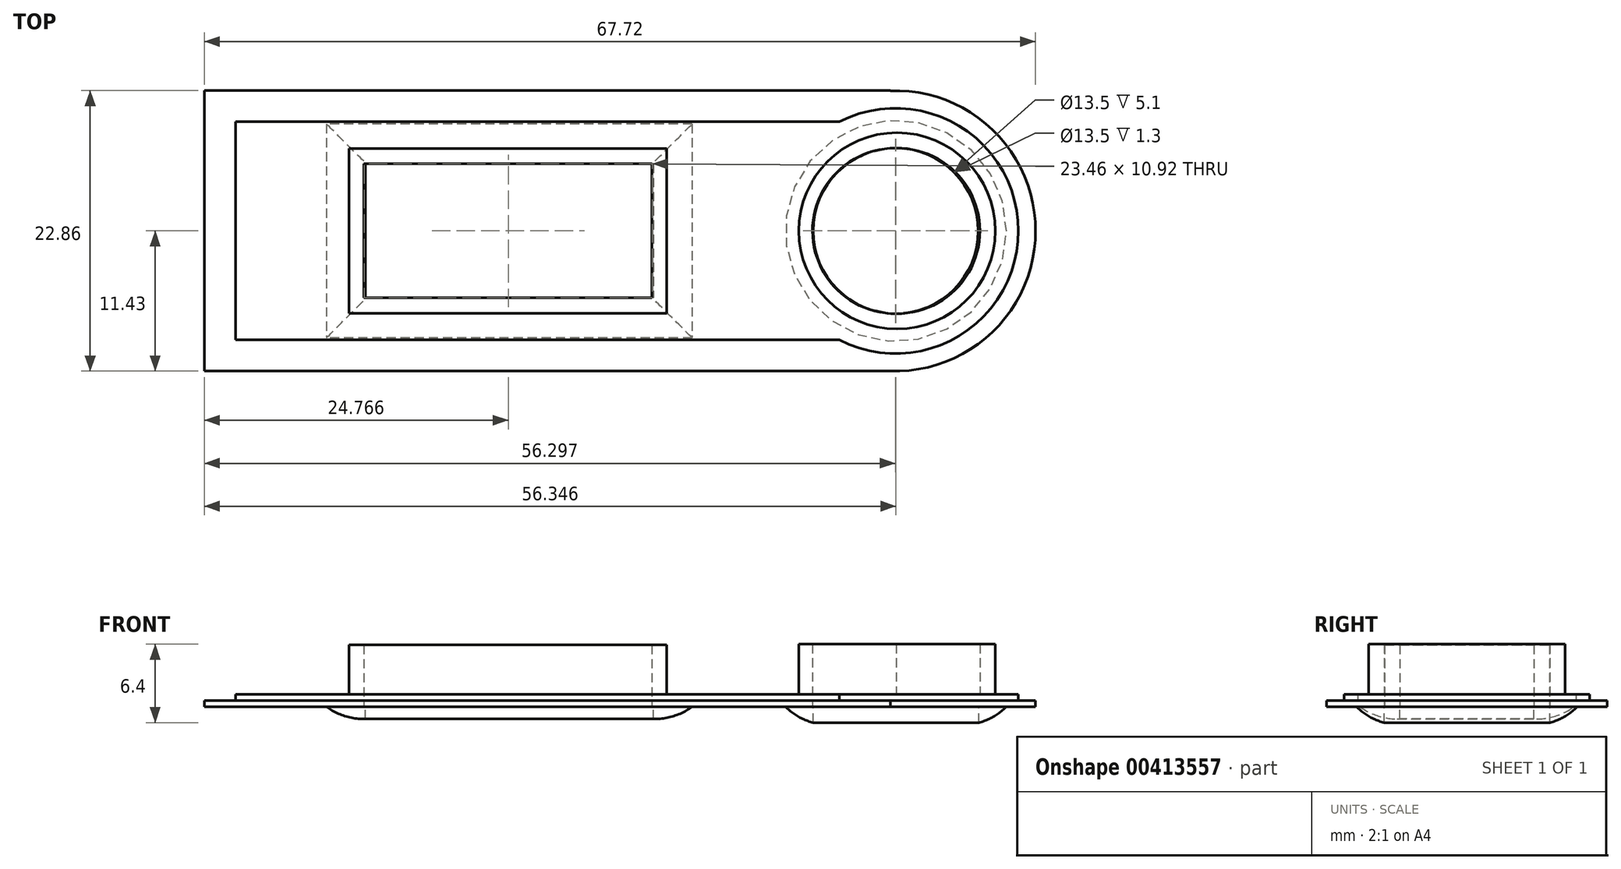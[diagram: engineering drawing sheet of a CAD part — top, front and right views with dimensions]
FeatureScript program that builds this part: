
annotation { "Feature Type Name" : "Feature", "Feature Type Description" : "" }
export const myFeature = defineFeature(function(context is Context, id is Id, definition is map)
    precondition{}
    {
        {
            var Q0;
            Q0=qCreatedBy(makeId("Top.planeOp"),FACE);
            var sketch = newSketch(context, id + "F0", { "sketchPlane" : qUnion([Q0])});
            skLineSegment(sketch, "E0.bottom", {"start": v(25.4, -8.9) * mm, "end": v(-25.4, -8.9) * mm});
            skLineSegment(sketch, "E0.top", {"start": v(25.4, 8.9) * mm, "end": v(-25.4, 8.89) * mm});
            skLineSegment(sketch, "E0.left", {"start": v(25.4, -8.9) * mm, "end": v(25.4, 8.9) * mm});
            skLineSegment(sketch, "E0.right", {"start": v(-25.4, -8.9) * mm, "end": v(-25.4, 8.89) * mm});
            skPoint(sketch, "E0.middle", {"position": v(0, 0) * mm});
            skSolve(sketch);
        }
        {
            var Q0;
            Q0=qCreatedBy(makeId("Top.planeOp"),FACE);
            var sketch = newSketch(context, id + "F1", { "sketchPlane" : qUnion([Q0])});
            skCircle(sketch, "E1", {"center": v(28.38, 0) * mm, "radius": 10 * mm});
            skSolve(sketch);
        }
        {
            var Q0;
            Q0=qSketchRegion(id+"F0",true);
            var Q1;
            Q1=qSketchRegion(id+"F18",true);
            extrude(context, id + "F2", {"entities" : qUnion([Q0, Q1]), "depth" : 1.02 * mm});
        }
        {
            var Q0;
            Q0=makeQuery(id+"F1.imprint","IMPRINT",FACE,{"disambiguationData":[TD([[makeQuery(id+"F1.imprint","IMPRINT",EDGE,{"derivedFrom":sQuery(id+"F1.wireOp",EDGE,"E1")}),1.0]])]});
            extrude(context, id + "F3", {"entities" : qUnion([Q0]), "operationType" : NewBodyOperationType.ADD, "depth" : 1.02 * mm});
        }
        {
            var Q0;
            Q0=qCreatedBy(makeId("Top.planeOp"),FACE);
            var sketch = newSketch(context, id + "F4", { "sketchPlane" : qUnion([Q0])});
            skCircle(sketch, "E2", {"center": v(28.36, 0) * mm, "radius": 6.75 * mm});
            skSolve(sketch);
        }
        {
            var Q0;
            Q0=qCreatedBy(makeId("Top.planeOp"),FACE);
            var sketch = newSketch(context, id + "F5", { "sketchPlane" : qUnion([Q0])});
            skLineSegment(sketch, "E3.bottom", {"start": v(27.94, -11.43) * mm, "end": v(-27.94, -11.43) * mm});
            skLineSegment(sketch, "E3.top", {"start": v(27.94, 11.43) * mm, "end": v(-27.94, 11.43) * mm});
            skLineSegment(sketch, "E3.left", {"start": v(27.94, -11.43) * mm, "end": v(27.94, 11.43) * mm});
            skLineSegment(sketch, "E3.right", {"start": v(-27.94, -11.43) * mm, "end": v(-27.94, 11.43) * mm});
            skPoint(sketch, "E3.middle", {"position": v(0, 0) * mm});
            skSolve(sketch);
        }
        {
            var Q0;
            Q0=qCreatedBy(makeId("Top.planeOp"),FACE);
            var sketch = newSketch(context, id + "F6", { "sketchPlane" : qUnion([Q0])});
            skCircle(sketch, "E4", {"center": v(28.35, 0) * mm, "radius": 11.43 * mm});
            skSolve(sketch);
        }
        {
            var Q0;
            Q0=makeQuery(id+"F5.imprint","IMPRINT",FACE,{"disambiguationData":[TD([[makeQuery(id+"F5.imprint","IMPRINT",EDGE,{"derivedFrom":sQuery(id+"F5.wireOp",EDGE,"E3.bottom")}),-1.0]])]});
            extrude(context, id + "F7", {"entities" : qUnion([Q0]), "operationType" : NewBodyOperationType.ADD, "depth" : 0.5 * mm});
        }
        {
            var Q0;
            Q0=makeQuery(id+"F6.imprint","IMPRINT",FACE,{"disambiguationData":[TD([[makeQuery(id+"F6.imprint","IMPRINT",EDGE,{"derivedFrom":sQuery(id+"F6.wireOp",EDGE,"E4")}),1.0]])]});
            extrude(context, id + "F8", {"entities" : qUnion([Q0]), "operationType" : NewBodyOperationType.ADD, "depth" : 0.5 * mm});
        }
        {
            var Q0;
            Q0=qCreatedBy(makeId("Top.planeOp"),FACE);
            var sketch = newSketch(context, id + "F9", { "sketchPlane" : qUnion([Q0])});
            skCircle(sketch, "E5", {"center": v(28.5, 0) * mm, "radius": 6.75 * mm});
            skCircle(sketch, "E6", {"center": v(28.5, 0) * mm, "radius": 8 * mm});
            skSolve(sketch);
        }
        {
            var Q0;
            Q0=makeQuery(id+"F9.imprint","IMPRINT",FACE,{"disambiguationData":[TD([[makeQuery(id+"F9.imprint","IMPRINT",EDGE,{"derivedFrom":sQuery(id+"F9.wireOp",EDGE,"E5")}),-1.0]])]});
            extrude(context, id + "F10", {"entities" : qUnion([Q0]), "operationType" : NewBodyOperationType.ADD, "depth" : 5.1 * mm});
        }
        {
            var Q0;
            Q0=sQuery(id+"F4.wireOp",VERTEX,"E2.center");
            var Q1;
            Q1=makeQuery(id+"F2.opExtrude","SWEPT_BODY",BODY,{"disambiguationData":[OSD([sQuery(id+"F0.wireOp",EDGE,"E0.bottom"),sQuery(id+"F0.wireOp",EDGE,"E0.top"),sQuery(id+"F0.wireOp",EDGE,"E0.left"),sQuery(id+"F0.wireOp",EDGE,"E0.right")])]});
            hole(context, id + "F11", {"style" : HoleStyle.SIMPLE, "endStyle" : HoleEndStyle.THROUGH, "oppositeDirection" : true, "holeDiameter" : 13.5 * mm, "isTappedThrough" : true, "tappedDepth" : 12 * mm, "tapClearance" : 3, "locations" : qUnion([Q0]), "scope" : qUnion([Q1])});
        }
        {
            var Q0;
            Q0=qCreatedBy(makeId("Top.planeOp"),FACE);
            var sketch = newSketch(context, id + "F12", { "sketchPlane" : qUnion([Q0])});
            skCircle(sketch, "E7", {"center": v(28.4, 0) * mm, "radius": 6.75 * mm});
            skCircle(sketch, "E8", {"center": v(28.4, 0) * mm, "radius": 9 * mm});
            skSolve(sketch);
        }
        {
            var Q0;
            Q0=makeQuery(id+"F12.imprint","IMPRINT",FACE,{"disambiguationData":[TD([[makeQuery(id+"F12.imprint","IMPRINT",EDGE,{"derivedFrom":sQuery(id+"F12.wireOp",EDGE,"E7")}),-1.0]])]});
            extrude(context, id + "F13", {"entities" : qUnion([Q0]), "operationType" : NewBodyOperationType.ADD, "oppositeDirection" : true, "depth" : 1.3 * mm});
        }
        {
            var Q0;
            Q0=qCreatedBy(makeId("Top.planeOp"),FACE);
            var sketch = newSketch(context, id + "F14", { "sketchPlane" : qUnion([Q0])});
            skLineSegment(sketch, "E9.bottom", {"start": v(8.56, -5.46) * mm, "end": v(-14.9, -5.46) * mm});
            skLineSegment(sketch, "E9.top", {"start": v(8.56, 5.46) * mm, "end": v(-14.9, 5.46) * mm});
            skLineSegment(sketch, "E9.left", {"start": v(8.56, -5.46) * mm, "end": v(8.56, 5.46) * mm});
            skLineSegment(sketch, "E9.right", {"start": v(-14.9, -5.46) * mm, "end": v(-14.9, 5.46) * mm});
            skPoint(sketch, "E9.middle", {"position": v(-3.17, 0) * mm});
            skSolve(sketch);
        }
        {
            var Q0;
            Q0=qSketchRegion(id+"F14",true);
            extrude(context, id + "F15", {"entities" : qUnion([Q0]), "operationType" : NewBodyOperationType.REMOVE, "endBound" : BoundingType.SYMMETRIC, "oppositeDirection" : true, "depth" : 66.04 * mm});
        }
        {
            var Q0;
            Q0=qCreatedBy(makeId("Top.planeOp"),FACE);
            var sketch = newSketch(context, id + "F16", { "sketchPlane" : qUnion([Q0])});
            skLineSegment(sketch, "E10.bottom", {"start": v(11.8, 8.71) * mm, "end": v(-17.98, 8.71) * mm});
            skLineSegment(sketch, "E10.top", {"start": v(11.8, -8.71) * mm, "end": v(-17.98, -8.71) * mm});
            skLineSegment(sketch, "E10.left", {"start": v(11.8, 8.71) * mm, "end": v(11.8, -8.71) * mm});
            skLineSegment(sketch, "E10.right", {"start": v(-17.98, 8.71) * mm, "end": v(-17.98, -8.71) * mm});
            skPoint(sketch, "E10.middle", {"position": v(-3.09, 0) * mm});
            skLineSegment(sketch, "E11.bottom", {"start": v(8.64, 5.46) * mm, "end": v(-14.82, 5.46) * mm});
            skLineSegment(sketch, "E11.top", {"start": v(8.64, -5.46) * mm, "end": v(-14.82, -5.46) * mm});
            skLineSegment(sketch, "E11.left", {"start": v(8.64, 5.46) * mm, "end": v(8.64, -5.46) * mm});
            skLineSegment(sketch, "E11.right", {"start": v(-14.82, 5.46) * mm, "end": v(-14.82, -5.46) * mm});
            skSolve(sketch);
        }
        {
            var Q0;
            Q0=makeQuery(id+"F16.imprint","IMPRINT",FACE,{"disambiguationData":[TD([[makeQuery(id+"F16.imprint","IMPRINT",EDGE,{"derivedFrom":sQuery(id+"F16.wireOp",EDGE,"E10.bottom")}),1.0]])]});
            extrude(context, id + "F17", {"entities" : qUnion([Q0]), "operationType" : NewBodyOperationType.ADD, "oppositeDirection" : true, "depth" : 1 * mm});
        }
        {
            var Q0;
            Q0=qCreatedBy(makeId("Top.planeOp"),FACE);
            var sketch = newSketch(context, id + "F18", { "sketchPlane" : qUnion([Q0])});
            skLineSegment(sketch, "E12.bottom", {"start": v(9.74, -6.7) * mm, "end": v(-16.16, -6.7) * mm});
            skLineSegment(sketch, "E12.top", {"start": v(9.74, 6.7) * mm, "end": v(-16.16, 6.7) * mm});
            skLineSegment(sketch, "E12.left", {"start": v(9.74, -6.7) * mm, "end": v(9.74, 6.7) * mm});
            skLineSegment(sketch, "E12.right", {"start": v(-16.16, -6.7) * mm, "end": v(-16.16, 6.7) * mm});
            skPoint(sketch, "E12.middle", {"position": v(-3.2, 0) * mm});
            skLineSegment(sketch, "E13.bottom", {"start": v(8.52, -5.46) * mm, "end": v(-14.94, -5.46) * mm});
            skLineSegment(sketch, "E13.top", {"start": v(8.52, 5.46) * mm, "end": v(-14.94, 5.46) * mm});
            skLineSegment(sketch, "E13.left", {"start": v(8.52, -5.46) * mm, "end": v(8.52, 5.46) * mm});
            skLineSegment(sketch, "E13.right", {"start": v(-14.94, -5.46) * mm, "end": v(-14.94, 5.46) * mm});
            skSolve(sketch);
        }
        {
            var Q0;
            Q0=makeQuery(id+"F18.imprint","IMPRINT",FACE,{"disambiguationData":[TD([[makeQuery(id+"F18.imprint","IMPRINT",EDGE,{"derivedFrom":sQuery(id+"F18.wireOp",EDGE,"E12.bottom")}),-1.0]])]});
            extrude(context, id + "F19", {"entities" : qUnion([Q0]), "depth" : 5.03 * mm});
        }
        {
            var Q0;
            Q0=makeQuery(id+"F17.opExtrude","CAP_EDGE",EDGE,{"disambiguationData":[OSD([sQuery(id+"F16.wireOp",EDGE,"E10.bottom")])],"isStart":false});
            fillet(context, id + "F20", {"entities" : qUnion([Q0]), "radius" : 5.08 * mm, "tangentPropagation" : true, "allowEdgeOverflow" : false});
        }
        {
            var Q0;
            Q0=makeQuery(id+"F17.opExtrude","CAP_EDGE",EDGE,{"disambiguationData":[OSD([sQuery(id+"F16.wireOp",EDGE,"E10.top")])],"isStart":false});
            fillet(context, id + "F21", {"entities" : qUnion([Q0]), "radius" : 5.08 * mm, "tangentPropagation" : true, "allowEdgeOverflow" : false});
        }
        {
            var Q0;
            Q0=makeQuery(id+"F17.opExtrude","CAP_EDGE",EDGE,{"disambiguationData":[OSD([sQuery(id+"F16.wireOp",EDGE,"E10.right")])],"isStart":false});
            fillet(context, id + "F22", {"entities" : qUnion([Q0]), "radius" : 5.08 * mm, "tangentPropagation" : true, "allowEdgeOverflow" : false});
        }
        {
            var Q0;
            Q0=makeQuery(id+"F17.opExtrude","CAP_EDGE",EDGE,{"disambiguationData":[OSD([sQuery(id+"F16.wireOp",EDGE,"E10.left")])],"isStart":false});
            fillet(context, id + "F23", {"entities" : qUnion([Q0]), "radius" : 5.08 * mm, "tangentPropagation" : true, "allowEdgeOverflow" : false});
        }
        {
            var Q0;
            Q0=makeQuery(id+"F13.opExtrude","CAP_EDGE",EDGE,{"disambiguationData":[OSD([sQuery(id+"F12.wireOp",EDGE,"E8")])],"isStart":false});
            fillet(context, id + "F24", {"entities" : qUnion([Q0]), "radius" : 5.08 * mm, "tangentPropagation" : true, "rho" : 0.5, "crossSection" : FilletCrossSection.CONIC, "allowEdgeOverflow" : false});
        }
    });
